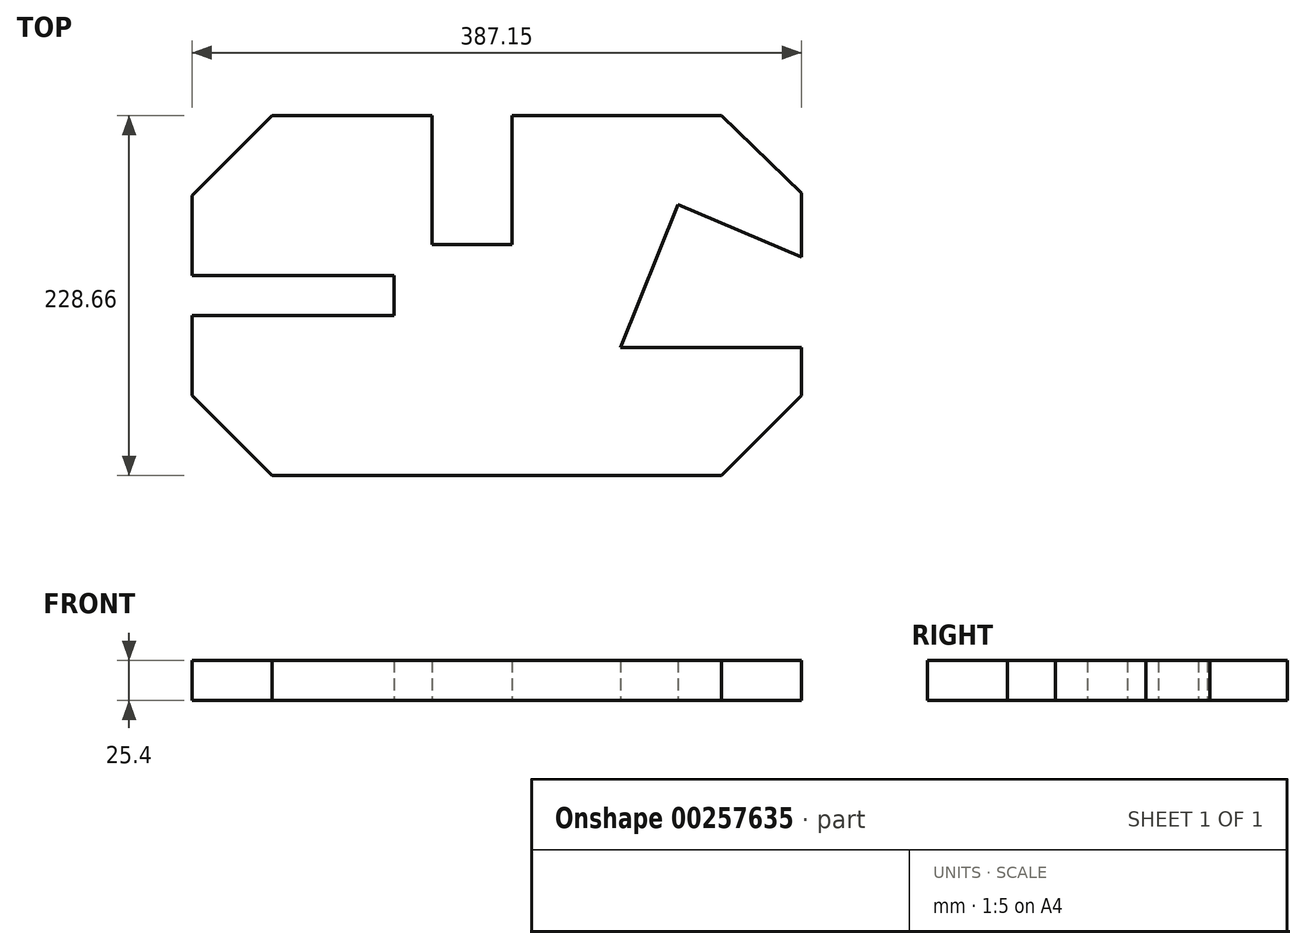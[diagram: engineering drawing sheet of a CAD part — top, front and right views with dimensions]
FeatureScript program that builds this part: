
annotation { "Feature Type Name" : "Feature", "Feature Type Description" : "" }
export const myFeature = defineFeature(function(context is Context, id is Id, definition is map)
    precondition{}
    {
        {
            var Q0;
            Q0=qCreatedBy(makeId("Top.planeOp"),FACE);
            var sketch = newSketch(context, id + "F0", { "sketchPlane" : qUnion([Q0])});
            skLineSegment(sketch, "E0", {"start": v(-92.63, -62.25) * mm, "end": v(192.86, -62.25) * mm});
            skLineSegment(sketch, "E1", {"start": v(192.86, -62.25) * mm, "end": v(243.7, -11.42) * mm});
            skLineSegment(sketch, "E2", {"start": v(-92.63, -62.25) * mm, "end": v(-143.46, -11.42) * mm});
            skLineSegment(sketch, "E3", {"start": v(243.7, -11.42) * mm, "end": v(243.7, 19.06) * mm});
            skLineSegment(sketch, "E4", {"start": v(243.7, 19.06) * mm, "end": v(128.63, 19.06) * mm});
            skLineSegment(sketch, "E5", {"start": v(128.63, 19.06) * mm, "end": v(165.26, 109.73) * mm});
            skLineSegment(sketch, "E6", {"start": v(165.26, 109.73) * mm, "end": v(243.7, 76.44) * mm});
            skLineSegment(sketch, "E7", {"start": v(243.7, 76.44) * mm, "end": v(243.7, 117.08) * mm});
            skLineSegment(sketch, "E8", {"start": v(243.7, 117.08) * mm, "end": v(192.86, 166.41) * mm});
            skLineSegment(sketch, "E9", {"start": v(192.86, 166.41) * mm, "end": v(59.77, 166.41) * mm});
            skLineSegment(sketch, "E10", {"start": v(59.77, 166.41) * mm, "end": v(59.77, 84.37) * mm});
            skLineSegment(sketch, "E11", {"start": v(59.77, 84.37) * mm, "end": v(8.97, 84.37) * mm});
            skLineSegment(sketch, "E12", {"start": v(8.97, 84.37) * mm, "end": v(8.97, 166.41) * mm});
            skLineSegment(sketch, "E13", {"start": v(8.97, 166.41) * mm, "end": v(-92.63, 166.41) * mm});
            skLineSegment(sketch, "E14", {"start": v(-92.63, 166.41) * mm, "end": v(-143.46, 115.58) * mm});
            skLineSegment(sketch, "E15", {"start": v(-143.46, 115.58) * mm, "end": v(-143.46, 64.78) * mm});
            skLineSegment(sketch, "E16", {"start": v(-143.46, 64.78) * mm, "end": v(-15.2, 64.78) * mm});
            skLineSegment(sketch, "E17", {"start": v(-15.2, 64.78) * mm, "end": v(-15.2, 39.38) * mm});
            skLineSegment(sketch, "E18", {"start": v(-15.2, 39.38) * mm, "end": v(-143.46, 39.38) * mm});
            skLineSegment(sketch, "E19", {"start": v(-143.46, 39.38) * mm, "end": v(-143.46, -11.42) * mm});
            skSolve(sketch);
        }
        {
            var Q0;
            Q0 = qSketchRegion(id + "F0", true);
            extrude(context, id + "F1", {"entities" : qUnion([Q0]), "depth" : 25.4 * mm});
        }
    });
